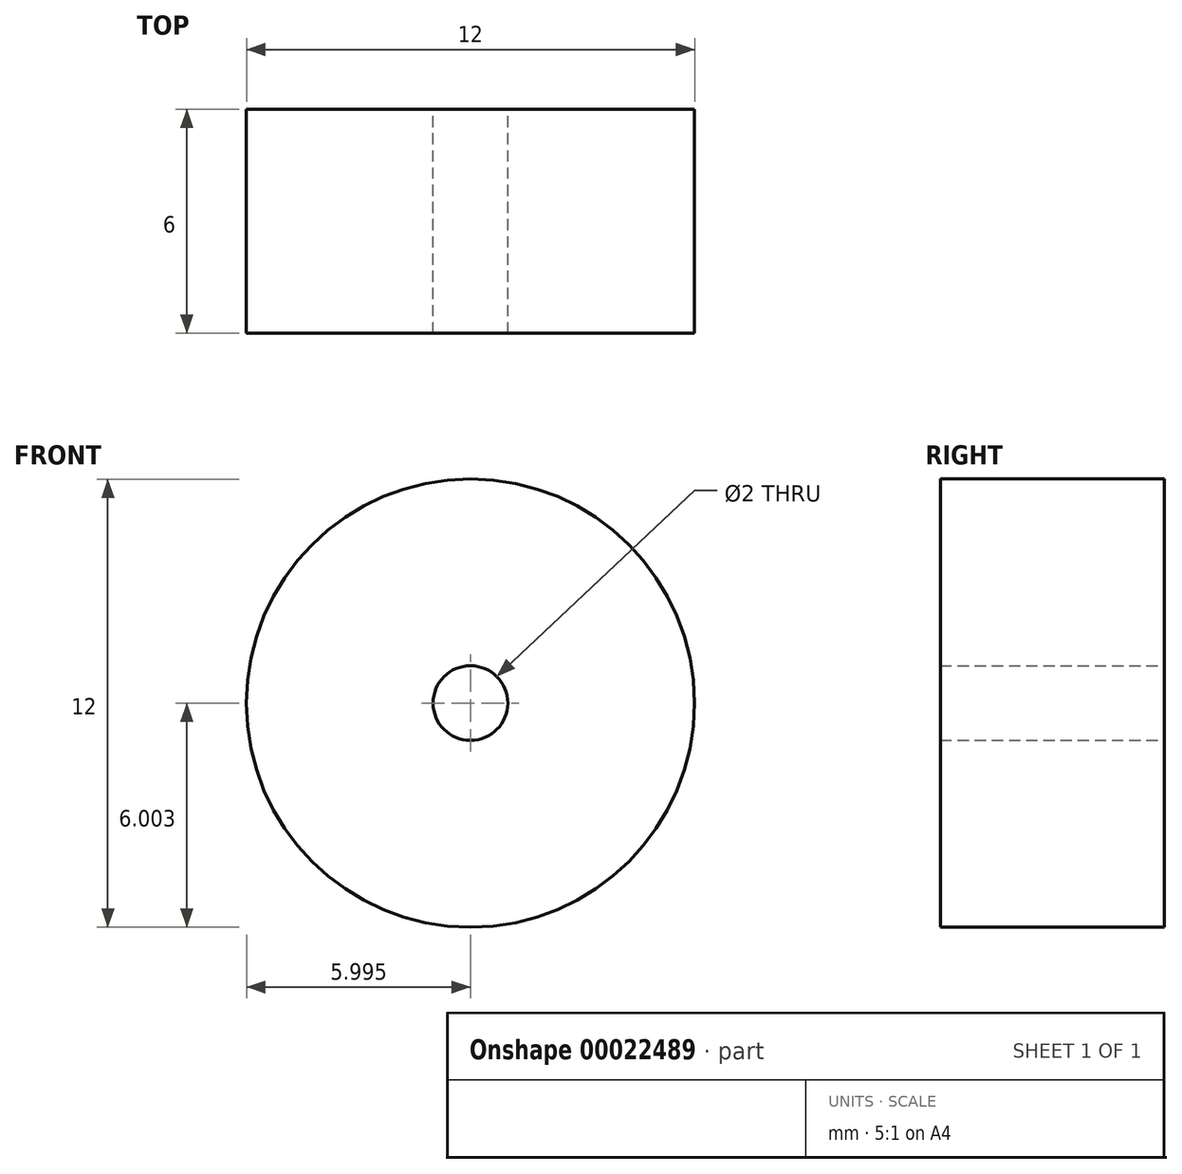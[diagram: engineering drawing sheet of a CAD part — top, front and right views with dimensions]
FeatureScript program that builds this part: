
annotation { "Feature Type Name" : "Feature", "Feature Type Description" : "" }
export const myFeature = defineFeature(function(context is Context, id is Id, definition is map)
    precondition{}
    {
        {
            var Q0;
            Q0=qCreatedBy(makeId("Front.planeOp"),FACE);
            var sketch = newSketch(context, id + "F0", { "sketchPlane" : qUnion([Q0])});
            skCircle(sketch, "E0", {"center": v(-35.65, 6.44) * mm, "radius": 6 * mm});
            skSolve(sketch);
        }
        {
            var Q0;
            Q0=makeQuery(id+"F0.imprint","IMPRINT",FACE,{"disambiguationData":[TD([[makeQuery(id+"F0.imprint","IMPRINT",EDGE,{"derivedFrom":sQuery(id+"F0.wireOp",EDGE,"E0")}),1.0]])]});
            extrude(context, id + "F1", {"entities" : qUnion([Q0]), "depth" : 6 * mm});
        }
        {
            var Q0;
            Q0=makeQuery(id+"F1.opExtrude","CAP_FACE",FACE,{"disambiguationData":[OSD([sQuery(id+"F0.wireOp",EDGE,"E0")])],"isStart":true});
            var sketch = newSketch(context, id + "F2", { "sketchPlane" : qUnion([Q0])});
            skCircle(sketch, "E1", {"center": v(35.65, 6.44) * mm, "radius": 1 * mm});
            skSolve(sketch);
        }
        {
            var Q0;
            Q0=makeQuery(id+"F2.imprint","IMPRINT",FACE,{"disambiguationData":[TD([[makeQuery(id+"F2.imprint","IMPRINT",EDGE,{"derivedFrom":sQuery(id+"F2.wireOp",EDGE,"E1")}),1.0]])]});
            extrude(context, id + "F3", {"entities" : qUnion([Q0]), "operationType" : NewBodyOperationType.REMOVE, "endBound" : BoundingType.THROUGH_ALL, "oppositeDirection" : true, "depth" : 2 * mm});
        }
    });
